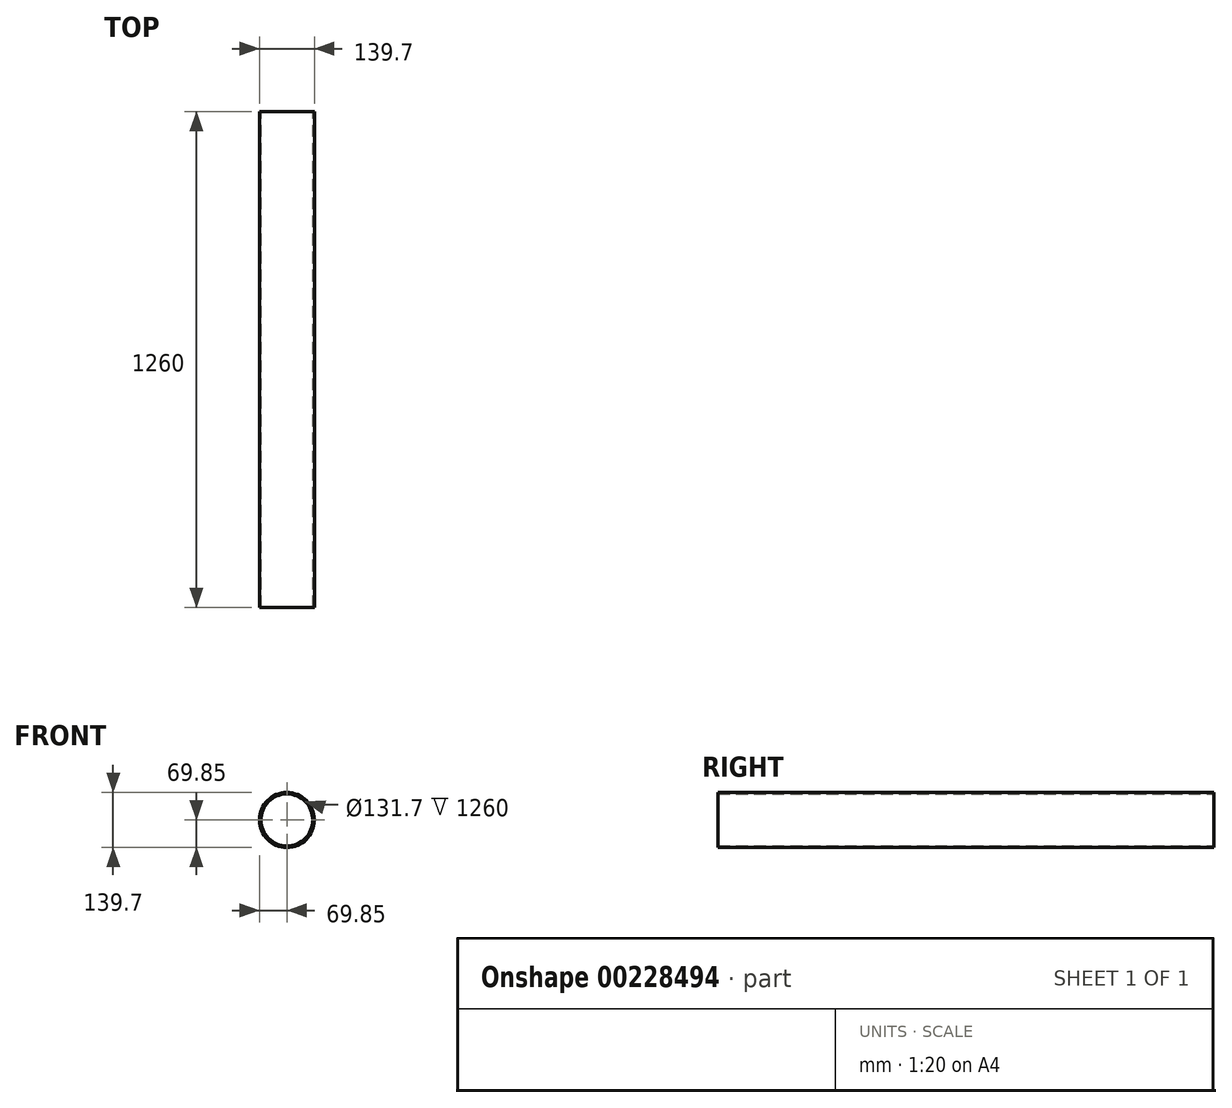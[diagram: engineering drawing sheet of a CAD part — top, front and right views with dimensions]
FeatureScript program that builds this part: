
annotation { "Feature Type Name" : "Feature", "Feature Type Description" : "" }
export const myFeature = defineFeature(function(context is Context, id is Id, definition is map)
    precondition{}
    {
        {
            assignVariable(context, id + "F0", {"name" : "L", "anyValue" : 1260});
        }
        {
            var Q0;
            Q0=qCreatedBy(makeId("Front.planeOp"),FACE);
            var sketch = newSketch(context, id + "F1", { "sketchPlane" : qUnion([Q0])});
            skCircle(sketch, "E0", {"center": v(0, 0) * mm, "radius": 69.85 * mm});
            skCircle(sketch, "E1.0", {"center": v(0, 0) * mm, "radius": 65.85 * mm});
            skSolve(sketch);
        }
        {
            var Q0;
            Q0=makeQuery(id+"F1.imprint","IMPRINT",FACE,{"disambiguationData":[TD([[makeQuery(id+"F1.imprint","IMPRINT",EDGE,{"derivedFrom":sQuery(id+"F1.wireOp",EDGE,"E0")}),1.0]])]});
            extrude(context, id + "F2", {"entities" : qUnion([Q0]), "depth" : (getVariable(context, 'L')) * mm, "hasSecondDirection" : true, "secondDirectionOppositeDirection" : true, "secondDirectionDepth" : 25 * mm, "symmetric" : true});
        }
    });
